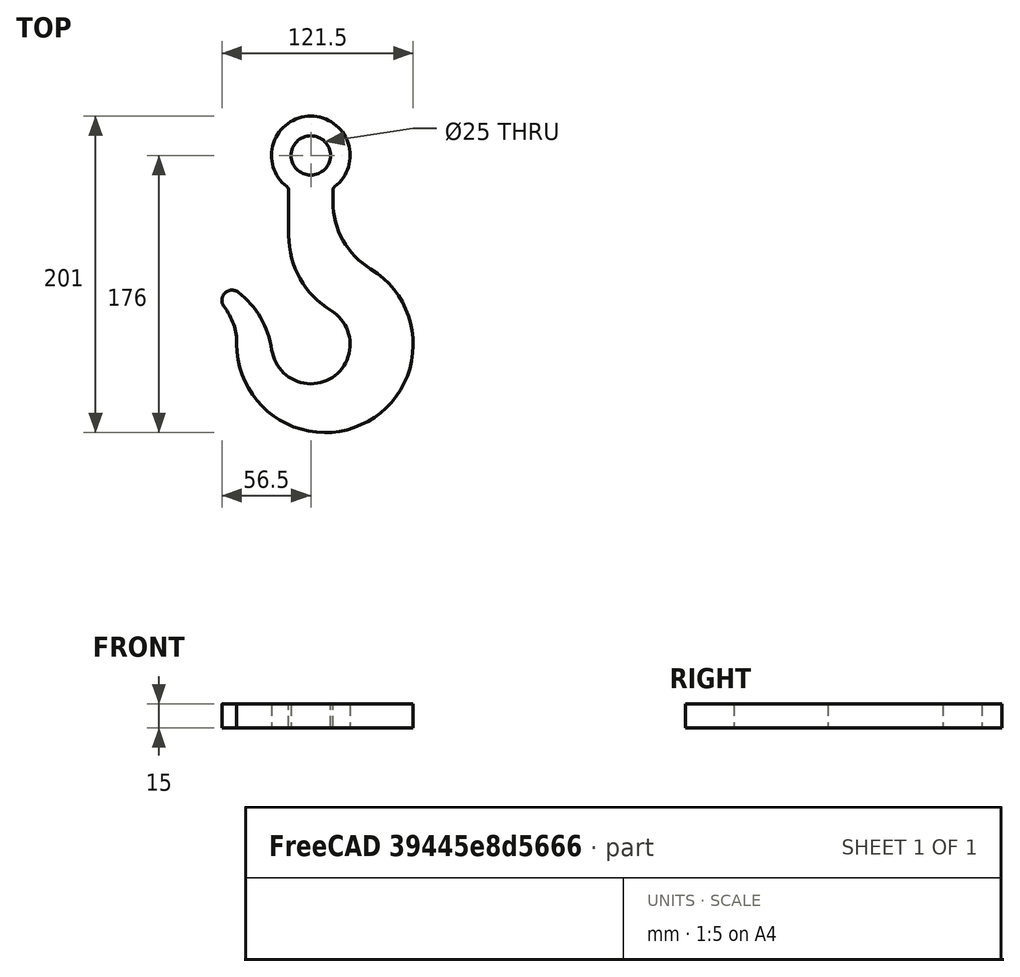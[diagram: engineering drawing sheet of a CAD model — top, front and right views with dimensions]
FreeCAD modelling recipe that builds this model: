
FCSTD DOCUMENT  (FreeCAD 1.0R39109 (Git))
Label: Задание 2-2
License: All rights reserved
LicenseURL: https://en.wikipedia.org/wiki/All_rights_reserved
objects: Sketcher::SketchObject×1, PartDesign::Pad×1, PartDesign::Body×1
note: 6 computed .brp shape members not serialized (recipe doc carries the construction recipe); baked Part::Feature solids carry a one-line shape summary decoded from their .brp

FEATURE [Sketcher::SketchObject] Sketch
  ArcFitTolerance = 1e-06
  AttachmentSupport = -> [XY_Plane]
  FullyConstrained = true
  MakeInternals = false
  MapMode = 5
  sketch-geometry (13):
    g0: Circle CenterX=0 CenterY=0 CenterZ=0 NormalX=0 NormalY=0 NormalZ=1 AngleXU=0 Radius=12.5
    g1: ArcOfCircle CenterX=0 CenterY=-120 CenterZ=0 NormalX=0 NormalY=0 NormalZ=1 AngleXU=0 Radius=25 StartAngle=3.28035 EndAngle=7.30886
    g2: ArcOfCircle CenterX=9 CenterY=-120 CenterZ=0 NormalX=0 NormalY=0 NormalZ=1 AngleXU=0 Radius=56 StartAngle=3.1361 EndAngle=7.30846
    g3: ArcOfCircle CenterX=-50 CenterY=-92 CenterZ=0 NormalX=0 NormalY=0 NormalZ=1 AngleXU=0 Radius=6.5 StartAngle=0.914061 EndAngle=3.80729
    g4: ArcOfCircle CenterX=-80.2215 CenterY=-131.203 CenterZ=0 NormalX=0 NormalY=0 NormalZ=1 AngleXU=0 Radius=56 StartAngle=0.13876 EndAngle=0.914061
    g5: ArcOfCircle CenterX=-84.9986 CenterY=-119.484 CenterZ=0 NormalX=0 NormalY=0 NormalZ=1 AngleXU=0 Radius=38 StartAngle=6.27769 EndAngle=6.94888
    g6: ArcOfCircle CenterX=0 CenterY=0 CenterZ=0 NormalX=0 NormalY=0 NormalZ=1 AngleXU=0 Radius=25 StartAngle=5.36485 EndAngle=10.3431
    g7: LineSegment StartX=-14 StartY=-22.2486 StartZ=0 EndX=-14 EndY=-50.7396 EndZ=0
    g8: LineSegment StartX=14 StartY=-22.2486 StartZ=0 EndX=14 EndY=-29.3854 EndZ=0
    g9: ArcOfCircle CenterX=17 CenterY=-22.2486 CenterZ=0 NormalX=0 NormalY=0 NormalZ=1 AngleXU=0 Radius=3 StartAngle=2.22326 EndAngle=3.14159
    g10: ArcOfCircle CenterX=-17 CenterY=-22.2486 CenterZ=0 NormalX=0 NormalY=0 NormalZ=1 AngleXU=0 Radius=3 StartAngle=2e-16 EndAngle=0.918336
    g11: ArcOfCircle CenterX=64 CenterY=-29.3854 CenterZ=0 NormalX=0 NormalY=0 NormalZ=1 AngleXU=0 Radius=50 StartAngle=3.14159 EndAngle=4.16686
    g12: ArcOfCircle CenterX=42 CenterY=-50.7396 CenterZ=0 NormalX=0 NormalY=0 NormalZ=1 AngleXU=0 Radius=56 StartAngle=3.14159 EndAngle=4.16727
  constraints (35):
    c: Coincident(g0,g-1)
    c: Diameter(g0) = 25
    c: Diameter(g1) = 50
    c: PointOnObject(g1,g-2)
    c: DistanceY(g1,g0) = 120
    c: Diameter(g2) = 112
    c: DistanceX(g1,g2) = 9
    c: Diameter(g3) = 13
    c: DistanceY(g1,g3) = 28
    c: DistanceX(g3,g-1) = 50
    c: DistanceY(g2) = -120
    c: Radius(g4) = 56
    c: Tangent(g1,g4) = 1.5708
    c: Radius(g5) = 38
    c: Tangent(g2,g5) = 1.5708
    c: Tangent(g3,g5) = 1.5708
    c: Tangent(g3,g4) = -1.5708
    c: Diameter(g6) = 50
    c: Coincident(g6,g0)
    c: Vertical(g7)
    c: Vertical(g8)
    c: Radius(g9) = 3
    c: Tangent(g9,g6) = 1.5708
    c: Tangent(g8,g9) = -1.5708
    c: Radius(g10) = 3
    c: Tangent(g6,g10) = 1.5708
    c: Tangent(g7,g10) = 1.5708
    c: DistanceX(g0,g8) = 14
    c: DistanceX(g7,g0) = 14
    c: Tangent(g8,g11) = -1.5708
    c: Tangent(g2,g11) = 1.5708
    c: Tangent(g7,g12) = -1.5708
    c: Tangent(g1,g12) = 1.5708
    c: Radius(g11) = 50
    c: Radius(g12) = 56
FEATURE [PartDesign::Pad] Pad
  Direction = (0,0,1)
  Length = 15
  Length2 = 10
  Profile = -> Sketch
  ReferenceAxis = -> Sketch [N_Axis]
  Refine = true
  Suppressed = false
  Type = 0
FEATURE [PartDesign::Body] Body  label="Тело"
  AllowCompound = false
  Group = -> [Sketch,Pad]
  Origin = -> Origin
  Tip = -> Pad
